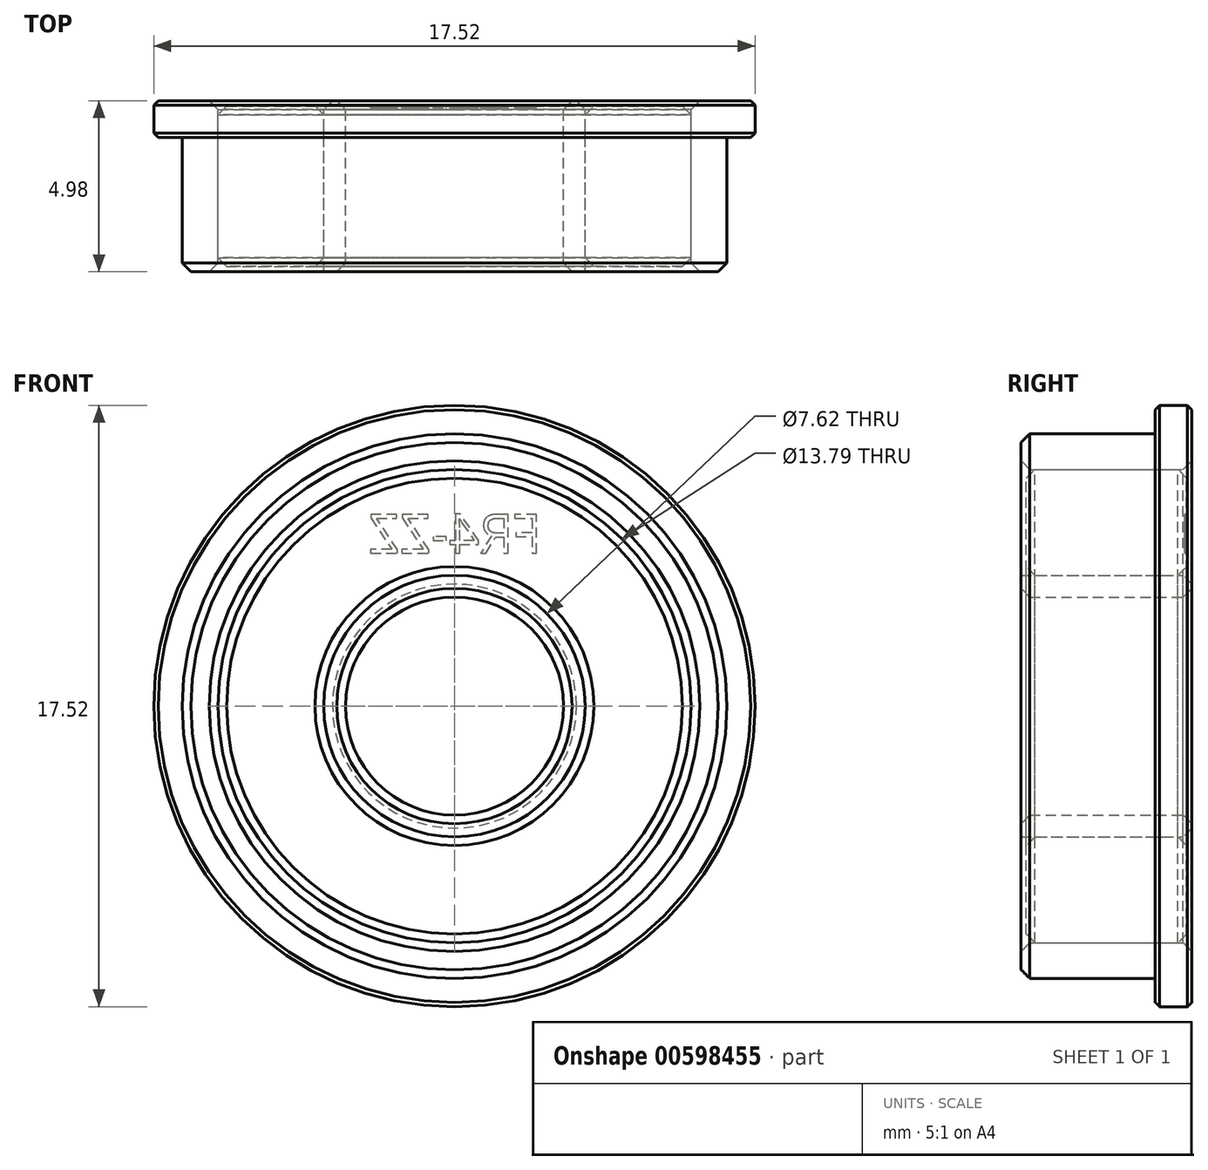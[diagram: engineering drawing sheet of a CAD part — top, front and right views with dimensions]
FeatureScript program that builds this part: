
annotation { "Feature Type Name" : "Feature", "Feature Type Description" : "" }
export const myFeature = defineFeature(function(context is Context, id is Id, definition is map)
    precondition{}
    {
        {
            var Q0;
            Q0=qCreatedBy(makeId("Front.planeOp"),FACE);
            var sketch = newSketch(context, id + "F0", { "sketchPlane" : qUnion([Q0])});
            skCircle(sketch, "E0", {"center": v(0, 0) * mm, "radius": 7.94 * mm});
            skCircle(sketch, "E1", {"center": v(0, 0) * mm, "radius": 6.9 * mm});
            skCircle(sketch, "E2", {"center": v(0, 0) * mm, "radius": 3.81 * mm});
            skCircle(sketch, "E3", {"center": v(0, 0) * mm, "radius": 3.18 * mm});
            skCircle(sketch, "E4", {"center": v(0, 0) * mm, "radius": 8.76 * mm});
            skSolve(sketch);
        }
        {
            var Q0;
            Q0=makeQuery(id+"F0.imprint","IMPRINT",FACE,{"disambiguationData":[TD([[makeQuery(id+"F0.imprint","IMPRINT",EDGE,{"derivedFrom":sQuery(id+"F0.wireOp",EDGE,"E0")}),-1.0]])]});
            extrude(context, id + "F1", {"entities" : qUnion([Q0]), "depth" : 1.07 * mm, "offsetDistance" : 25.4 * mm});
        }
        {
            var Q0;
            Q0=makeQuery(id+"F0.imprint","IMPRINT",FACE,{"disambiguationData":[TD([[makeQuery(id+"F0.imprint","IMPRINT",EDGE,{"derivedFrom":sQuery(id+"F0.wireOp",EDGE,"E2")}),1.0]])]});
            var Q1;
            Q1=makeQuery(id+"F0.imprint","IMPRINT",FACE,{"disambiguationData":[TD([[makeQuery(id+"F0.imprint","IMPRINT",EDGE,{"derivedFrom":sQuery(id+"F0.wireOp",EDGE,"E0")}),1.0]])]});
            extrude(context, id + "F2", {"entities" : qUnion([Q0, Q1]), "operationType" : NewBodyOperationType.ADD, "depth" : 4.98 * mm, "offsetDistance" : 25.4 * mm});
        }
        {
            var Q0;
            Q0=makeQuery(id+"F0.imprint","IMPRINT",FACE,{"disambiguationData":[TD([[makeQuery(id+"F0.imprint","IMPRINT",EDGE,{"derivedFrom":sQuery(id+"F0.wireOp",EDGE,"E1")}),1.0]])]});
            extrude(context, id + "F3", {"entities" : qUnion([Q0]), "depth" : 4.83 * mm, "offsetDistance" : 25.4 * mm});
        }
        {
            var Q0;
            Q0=makeQuery(id+"F0.imprint","IMPRINT",FACE,{"disambiguationData":[TD([[makeQuery(id+"F0.imprint","IMPRINT",EDGE,{"derivedFrom":sQuery(id+"F0.wireOp",EDGE,"E1")}),1.0]])]});
            extrude(context, id + "F4", {"entities" : qUnion([Q0]), "operationType" : NewBodyOperationType.REMOVE, "depth" : 0.15 * mm, "offsetDistance" : 25.4 * mm});
        }
        {
            var Q0;
            Q0=makeQuery(id+"F2.opExtrude","CAP_EDGE",EDGE,{"disambiguationData":[OSD([sQuery(id+"F0.wireOp",EDGE,"E0")])],"isStart":false});
            var Q1;
            Q1=makeQuery(id+"F2.opExtrude","CAP_EDGE",EDGE,{"disambiguationData":[OSD([sQuery(id+"F0.wireOp",EDGE,"E3")])],"isStart":false});
            var Q2;
            Q2=makeQuery(id+"F2.opExtrude","CAP_EDGE",EDGE,{"disambiguationData":[OSD([sQuery(id+"F0.wireOp",EDGE,"E1")])],"isStart":true});
            var Q3;
            Q3=makeQuery(id+"F2.opExtrude","CAP_EDGE",EDGE,{"disambiguationData":[OSD([sQuery(id+"F0.wireOp",EDGE,"E1")])],"isStart":false});
            var Q4;
            Q4=makeQuery(id+"F3.opExtrude","CAP_EDGE",EDGE,{"disambiguationData":[OSD([sQuery(id+"F0.wireOp",EDGE,"E2")])],"isStart":false});
            var Q5;
            Q5=makeQuery(id+"F2.opExtrude","CAP_EDGE",EDGE,{"disambiguationData":[OSD([sQuery(id+"F0.wireOp",EDGE,"E3")])],"isStart":true});
            var Q6;
            Q6=makeQuery(id+"F2.opExtrude","CAP_FACE",FACE,{"disambiguationData":[OSD([sQuery(id+"F0.wireOp",EDGE,"E2"),sQuery(id+"F0.wireOp",EDGE,"E3")])],"isStart":true});
            var Q7;
            Q7=makeQuery(id+"F4.boolean.opBoolean","COPY",EDGE,{"derivedFrom":makeQuery(id+"F4.opExtrude","CAP_EDGE",EDGE,{"disambiguationData":[OSD([sQuery(id+"F0.wireOp",EDGE,"E2")])],"isStart":false})});
            var Q8;
            Q8=makeQuery(id+"F4.boolean.opBoolean","COPY",FACE,{"derivedFrom":makeQuery(id+"F4.opExtrude","CAP_FACE",FACE,{"disambiguationData":[OSD([sQuery(id+"F0.wireOp",EDGE,"E1"),sQuery(id+"F0.wireOp",EDGE,"E2")])],"isStart":false})});
            var Q9;
            Q9=makeQuery(id+"F3.opExtrude","CAP_EDGE",EDGE,{"disambiguationData":[OSD([sQuery(id+"F0.wireOp",EDGE,"E1")])],"isStart":false});
            chamfer(context, id + "F5", {"entities" : qUnion([Q0, Q1, Q2, Q3, Q4, Q5, Q6, Q7, Q8, Q9]), "width" : 0.25 * mm, "tangentPropagation" : true});
        }
        {
            var Q0;
            Q0=makeQuery(id+"F1.opExtrude","CAP_EDGE",EDGE,{"disambiguationData":[OSD([sQuery(id+"F0.wireOp",EDGE,"E4")])],"isStart":false});
            var Q1;
            Q1=makeQuery(id+"F1.opExtrude","CAP_EDGE",EDGE,{"disambiguationData":[OSD([sQuery(id+"F0.wireOp",EDGE,"E4")])],"isStart":true});
            chamfer(context, id + "F6", {"entities" : qUnion([Q0, Q1]), "width" : 0.13 * mm, "tangentPropagation" : true});
        }
        {
            var Q0;
            Q0=makeQuery(id+"F4.boolean.opBoolean","COPY",FACE,{"derivedFrom":makeQuery(id+"F4.opExtrude","CAP_FACE",FACE,{"disambiguationData":[OSD([sQuery(id+"F0.wireOp",EDGE,"E1"),sQuery(id+"F0.wireOp",EDGE,"E2")])],"isStart":false})});
            var sketch = newSketch(context, id + "F7", { "sketchPlane" : qUnion([Q0])});
            skText(sketch, "E5", { "text": "FR4-ZZ", "fontName": "OpenSans-Regular.ttf"});
            skPoint(sketch, "E6", {"position": v(-6.14, 2.54) * mm});
            const initialGuessF7  = {"E5": [-0.00255, 0.00445, 1, 0, 0.00115]};
            skSetInitialGuess(sketch, initialGuessF7);
            skSolve(sketch);
        }
        {
            var Q0;
            Q0 = qSketchRegion(id + "F7", true);
            extrude(context, id + "F8", {"entities" : qUnion([Q0]), "operationType" : NewBodyOperationType.REMOVE, "oppositeDirection" : true, "depth" : 0.05 * mm, "offsetDistance" : 25.4 * mm});
        }
    });
